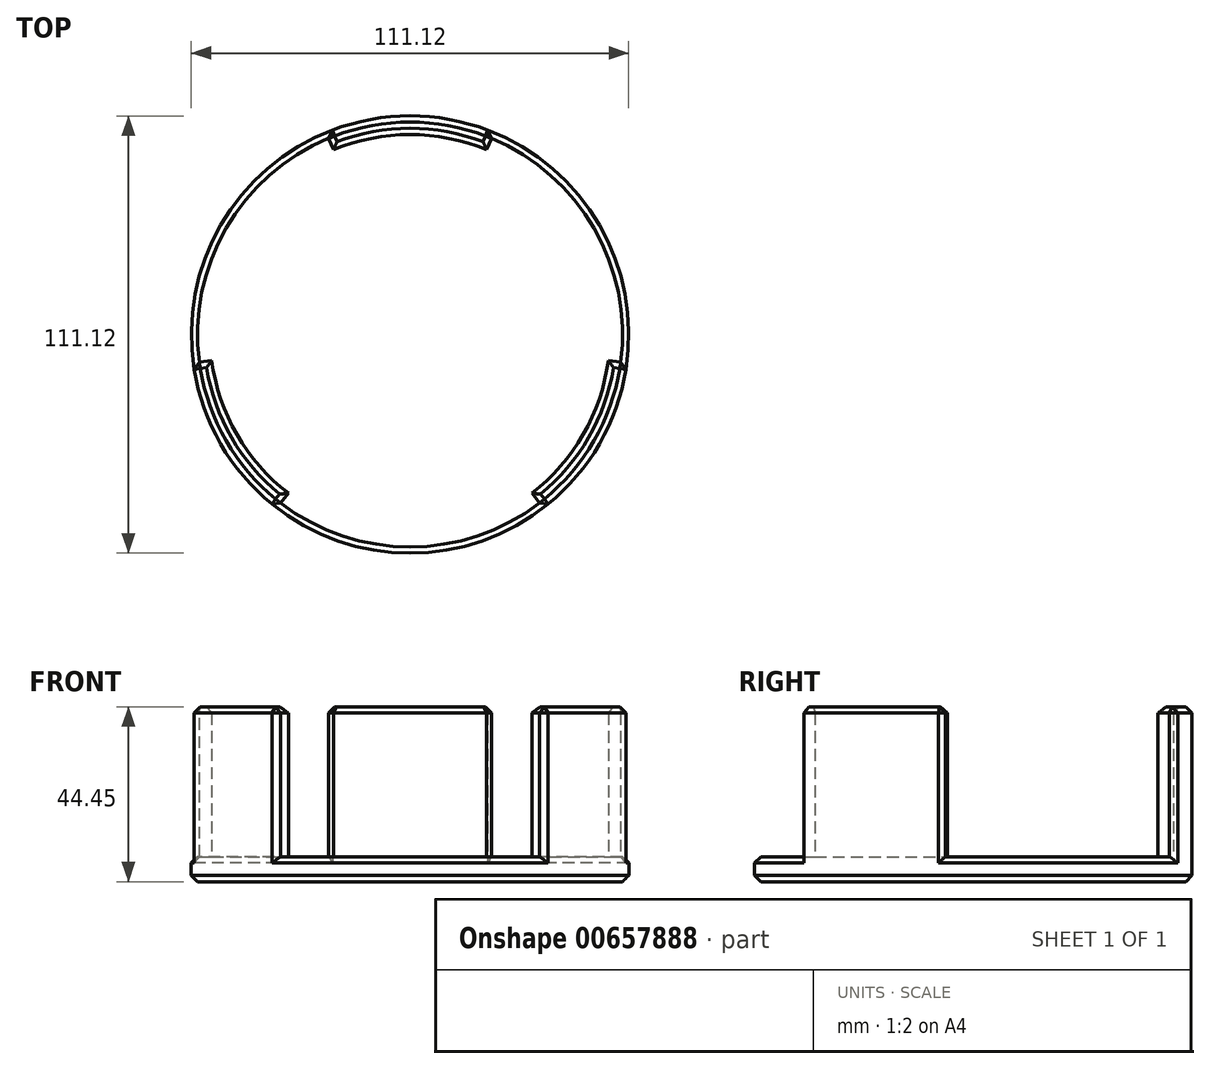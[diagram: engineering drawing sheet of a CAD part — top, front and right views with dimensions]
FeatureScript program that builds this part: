
annotation { "Feature Type Name" : "Feature", "Feature Type Description" : "" }
export const myFeature = defineFeature(function(context is Context, id is Id, definition is map)
    precondition{}
    {
        {
            var Q0;
            Q0=qCreatedBy(makeId("Top.planeOp"),FACE);
            var sketch = newSketch(context, id + "F0", { "sketchPlane" : qUnion([Q0])});
            skCircle(sketch, "E0", {"center": v(0, 0) * mm, "radius": 55.56 * mm});
            skSolve(sketch);
        }
        {
            var Q0;
            Q0=makeQuery(id+"F0.imprint","IMPRINT",FACE,{"disambiguationData":[TD([[makeQuery(id+"F0.imprint","IMPRINT",EDGE,{"derivedFrom":sQuery(id+"F0.wireOp",EDGE,"E0")}),1.0]])]});
            extrude(context, id + "F1", {"entities" : qUnion([Q0]), "depth" : 6.35 * mm, "offsetDistance" : 25.4 * mm});
        }
        {
            var Q0;
            Q0=makeQuery(id+"F1.opExtrude","CAP_FACE",FACE,{"disambiguationData":[OSD([sQuery(id+"F0.wireOp",EDGE,"E0")])],"isStart":false});
            var sketch = newSketch(context, id + "F2", { "sketchPlane" : qUnion([Q0])});
            skCircle(sketch, "E1.0", {"center": v(0, 0) * mm, "radius": 55.56 * mm, "construction": true});
            skCircle(sketch, "E2", {"center": v(0, 0) * mm, "radius": 50.8 * mm, "construction": true});
            skLineSegment(sketch, "E3", {"start": v(0, 0) * mm, "end": v(-21.26, 51.33) * mm, "construction": true});
            skLineSegment(sketch, "E4", {"start": v(0, 0) * mm, "end": v(21.26, 51.33) * mm, "construction": true});
            skLineSegment(sketch, "E5", {"start": v(0, 0) * mm, "end": v(55.09, -7.25) * mm, "construction": true});
            skLineSegment(sketch, "E6", {"start": v(0, 0) * mm, "end": v(33.82, -44.08) * mm, "construction": true});
            skLineSegment(sketch, "E7", {"start": v(0, 0) * mm, "end": v(-33.82, -44.08) * mm, "construction": true});
            skLineSegment(sketch, "E8", {"start": v(0, 0) * mm, "end": v(-55.09, -7.25) * mm, "construction": true});
            skArc(sketch, "E9", {"start": v(-21.26, 51.33) * mm, "mid": v(0, 55.56) * mm, "end": v(21.26, 51.33) * mm});
            skArc(sketch, "E10", {"start": v(-19.44, 46.93) * mm, "mid": v(0, 50.8) * mm, "end": v(19.44, 46.93) * mm});
            skArc(sketch, "E11", {"start": v(33.82, -44.08) * mm, "mid": v(48.12, -27.78) * mm, "end": v(55.09, -7.25) * mm});
            skArc(sketch, "E12", {"start": v(-30.93, -40.3) * mm, "mid": v(-44, -25.4) * mm, "end": v(-50.37, -6.63) * mm});
            skArc(sketch, "E13", {"start": v(-33.82, -44.08) * mm, "mid": v(-48.12, -27.78) * mm, "end": v(-55.09, -7.25) * mm});
            skArc(sketch, "E14", {"start": v(50.37, -6.63) * mm, "mid": v(44, -25.4) * mm, "end": v(30.93, -40.3) * mm});
            skLineSegment(sketch, "E15", {"start": v(-33.82, -44.08) * mm, "end": v(-30.93, -40.3) * mm});
            skLineSegment(sketch, "E16", {"start": v(-55.09, -7.25) * mm, "end": v(-50.37, -6.63) * mm});
            skLineSegment(sketch, "E17", {"start": v(30.93, -40.3) * mm, "end": v(33.82, -44.08) * mm});
            skLineSegment(sketch, "E18", {"start": v(50.37, -6.63) * mm, "end": v(55.09, -7.25) * mm});
            skLineSegment(sketch, "E19", {"start": v(-21.26, 51.33) * mm, "end": v(-19.44, 46.93) * mm});
            skLineSegment(sketch, "E20", {"start": v(21.26, 51.33) * mm, "end": v(19.44, 46.93) * mm});
            skSolve(sketch);
        }
        {
            var Q0;
            Q0 = qSketchRegion(id + "F2", true);
            extrude(context, id + "F3", {"entities" : qUnion([Q0]), "operationType" : NewBodyOperationType.ADD, "depth" : 38.1 * mm, "offsetDistance" : 25.4 * mm});
        }
        {
            var Q0;
            Q0=makeQuery(id+"F1.opExtrude","CAP_EDGE",EDGE,{"disambiguationData":[OSD([sQuery(id+"F0.wireOp",EDGE,"E0")])],"isStart":true});
            var Q1;
            Q1=makeQuery(id+"F3.opExtrude","CAP_EDGE",EDGE,{"disambiguationData":[OSD([sQuery(id+"F2.wireOp",EDGE,"E12")])],"isStart":true});
            var Q2;
            Q2=makeQuery(id+"F3.opExtrude","CAP_EDGE",EDGE,{"disambiguationData":[OSD([sQuery(id+"F2.wireOp",EDGE,"E10")])],"isStart":true});
            var Q3;
            Q3=makeQuery(id+"F3.opExtrude","CAP_EDGE",EDGE,{"disambiguationData":[OSD([sQuery(id+"F2.wireOp",EDGE,"E14")])],"isStart":true});
            var Q4;
            Q4=makeQuery(id+"F3.opExtrude","CAP_EDGE",EDGE,{"disambiguationData":[OSD([sQuery(id+"F2.wireOp",EDGE,"E13")])],"isStart":false});
            var Q5;
            Q5=makeQuery(id+"F3.opExtrude","CAP_EDGE",EDGE,{"disambiguationData":[OSD([sQuery(id+"F2.wireOp",EDGE,"E12")])],"isStart":false});
            var Q6;
            Q6=makeQuery(id+"F3.opExtrude","CAP_EDGE",EDGE,{"disambiguationData":[OSD([sQuery(id+"F2.wireOp",EDGE,"E15")])],"isStart":false});
            var Q7;
            Q7=makeQuery(id+"F3.opExtrude","CAP_EDGE",EDGE,{"disambiguationData":[OSD([sQuery(id+"F2.wireOp",EDGE,"E16")])],"isStart":false});
            var Q8;
            Q8=makeQuery(id+"F3.opExtrude","CAP_EDGE",EDGE,{"disambiguationData":[OSD([sQuery(id+"F2.wireOp",EDGE,"E17")])],"isStart":false});
            var Q9;
            Q9=makeQuery(id+"F3.opExtrude","CAP_EDGE",EDGE,{"disambiguationData":[OSD([sQuery(id+"F2.wireOp",EDGE,"E14")])],"isStart":false});
            var Q10;
            Q10=makeQuery(id+"F3.opExtrude","CAP_EDGE",EDGE,{"disambiguationData":[OSD([sQuery(id+"F2.wireOp",EDGE,"E11")])],"isStart":false});
            var Q11;
            Q11=makeQuery(id+"F3.opExtrude","CAP_EDGE",EDGE,{"disambiguationData":[OSD([sQuery(id+"F2.wireOp",EDGE,"E18")])],"isStart":false});
            var Q12;
            Q12=makeQuery(id+"F3.opExtrude","CAP_EDGE",EDGE,{"disambiguationData":[OSD([sQuery(id+"F2.wireOp",EDGE,"E10")])],"isStart":false});
            var Q13;
            Q13=makeQuery(id+"F3.opExtrude","CAP_FACE",FACE,{"disambiguationData":[OSD([sQuery(id+"F2.wireOp",EDGE,"E9"),sQuery(id+"F2.wireOp",EDGE,"E10"),sQuery(id+"F2.wireOp",EDGE,"E19"),sQuery(id+"F2.wireOp",EDGE,"E20")])],"isStart":false});
            var Q14;
            Q14=makeQuery(id+"F3.opExtrude","CAP_EDGE",EDGE,{"disambiguationData":[OSD([sQuery(id+"F2.wireOp",EDGE,"E20")])],"isStart":true});
            var Q15;
            Q15=makeQuery(id+"F3.opExtrude","CAP_EDGE",EDGE,{"disambiguationData":[OSD([sQuery(id+"F2.wireOp",EDGE,"E19")])],"isStart":true});
            var Q16;
            Q16=makeQuery(id+"F3.opExtrude","CAP_EDGE",EDGE,{"disambiguationData":[OSD([sQuery(id+"F2.wireOp",EDGE,"E17")])],"isStart":true});
            var Q17;
            Q17=makeQuery(id+"F3.opExtrude","CAP_EDGE",EDGE,{"disambiguationData":[OSD([sQuery(id+"F2.wireOp",EDGE,"E18")])],"isStart":true});
            var Q18;
            Q18=makeQuery(id+"F3.opExtrude","CAP_EDGE",EDGE,{"disambiguationData":[OSD([sQuery(id+"F2.wireOp",EDGE,"E15")])],"isStart":true});
            var Q19;
            Q19=makeQuery(id+"F3.opExtrude","CAP_EDGE",EDGE,{"disambiguationData":[OSD([sQuery(id+"F2.wireOp",EDGE,"E16")])],"isStart":true});
            var Q20;
            {var subQ0=sQuery(id+"F0.wireOp",EDGE,"E0");Q20=makeQuery(id+"F3.boolean.opBoolean","SPLIT",EDGE,{"disambiguationData":[TD([makeQuery(id+"F3.opExtrude","SWEPT_FACE",FACE,{"disambiguationData":[OSD([sQuery(id+"F2.wireOp",EDGE,"E15")])]})])],"derivedFrom":makeQuery(id+"F1.opExtrude","CAP_EDGE",EDGE,{"disambiguationData":[OSD([subQ0])],"isStart":false})});}
            var Q21;
            {var subQ0=sQuery(id+"F0.wireOp",EDGE,"E0");Q21=makeQuery(id+"F3.boolean.opBoolean","SPLIT",EDGE,{"disambiguationData":[TD([makeQuery(id+"F3.opExtrude","SWEPT_FACE",FACE,{"disambiguationData":[OSD([sQuery(id+"F2.wireOp",EDGE,"E18")])]})])],"derivedFrom":makeQuery(id+"F1.opExtrude","CAP_EDGE",EDGE,{"disambiguationData":[OSD([subQ0])],"isStart":false})});}
            var Q22;
            Q22=makeQuery(id+"F3.boolean.opBoolean","MERGE",FACE,{"derivedFrom":[makeQuery(id+"F1.opExtrude","SWEPT_FACE",FACE,{"disambiguationData":[OSD([sQuery(id+"F0.wireOp",EDGE,"E0")])]}),makeQuery(id+"F3.opExtrude","SWEPT_FACE",FACE,{"disambiguationData":[OSD([sQuery(id+"F2.wireOp",EDGE,"E9")])]}),makeQuery(id+"F3.opExtrude","SWEPT_FACE",FACE,{"disambiguationData":[OSD([sQuery(id+"F2.wireOp",EDGE,"E11")])]}),makeQuery(id+"F3.opExtrude","SWEPT_FACE",FACE,{"disambiguationData":[OSD([sQuery(id+"F2.wireOp",EDGE,"E13")])]})]});
            chamfer(context, id + "F4", {"entities" : qUnion([Q0, Q1, Q2, Q3, Q4, Q5, Q6, Q7, Q8, Q9, Q10, Q11, Q12, Q13, Q14, Q15, Q16, Q17, Q18, Q19, Q20, Q21, Q22]), "width" : 1.59 * mm, "tangentPropagation" : true});
        }
    });
